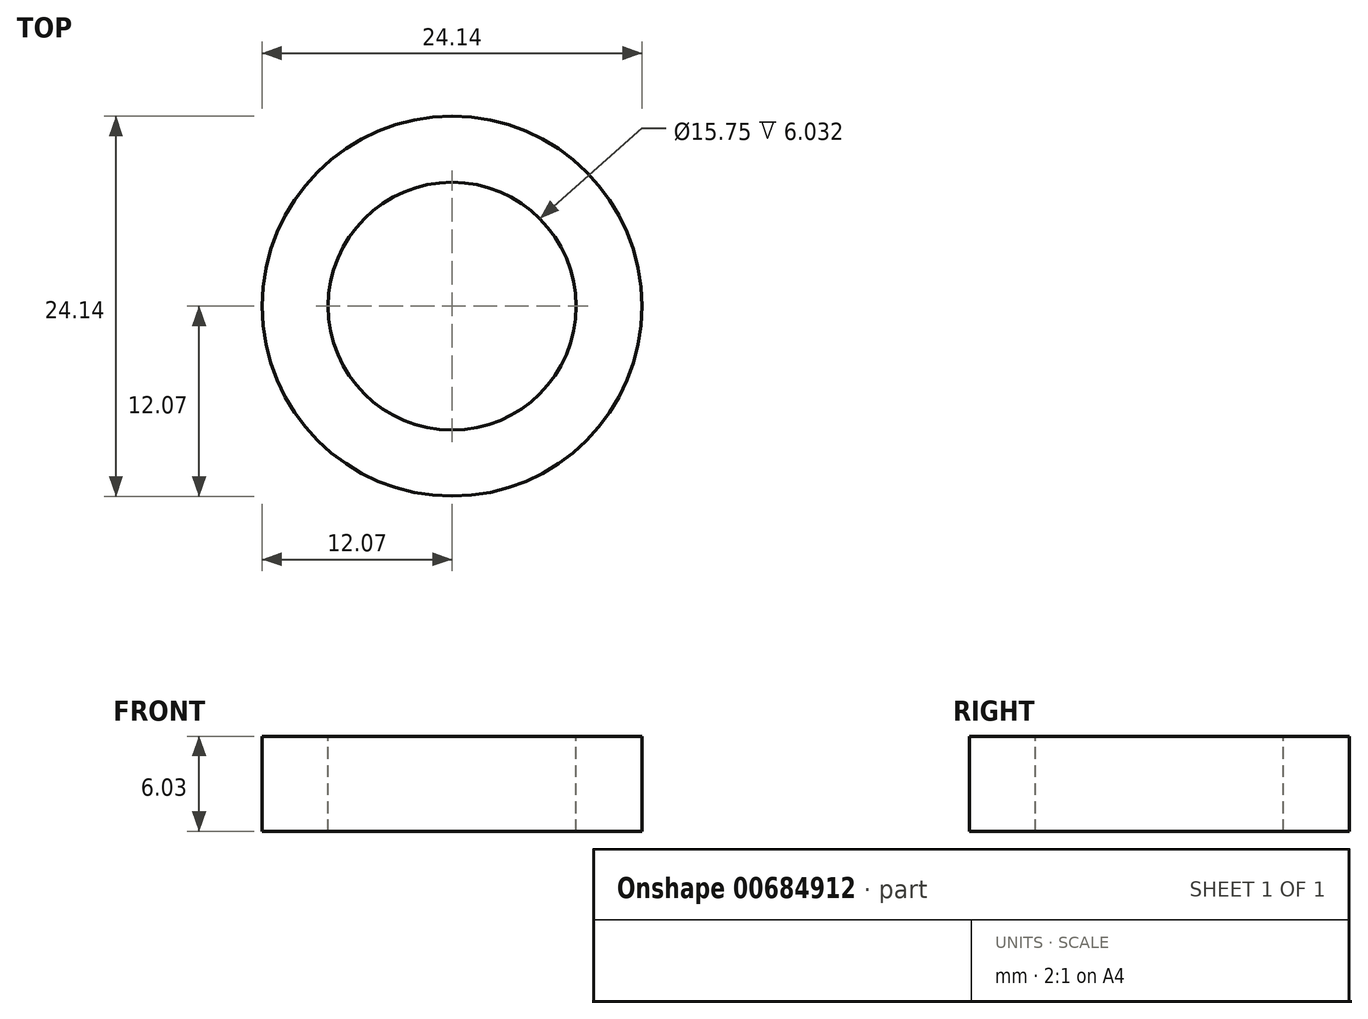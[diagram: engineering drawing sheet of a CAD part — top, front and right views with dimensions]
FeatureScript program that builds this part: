
annotation { "Feature Type Name" : "Feature", "Feature Type Description" : "" }
export const myFeature = defineFeature(function(context is Context, id is Id, definition is map)
    precondition{}
    {
        {
            var Q0;
            Q0=qCreatedBy(makeId("Front.planeOp"),FACE);
            var sketch = newSketch(context, id + "F0", { "sketchPlane" : qUnion([Q0])});
            skLineSegment(sketch, "E0", {"start": v(0, 45.28) * mm, "end": v(0, -44.75) * mm, "construction": true});
            skLineSegment(sketch, "E1", {"start": v(7.87, 0) * mm, "end": v(12.07, 0) * mm});
            skLineSegment(sketch, "E2", {"start": v(12.07, 0) * mm, "end": v(12.07, 6.03) * mm});
            skLineSegment(sketch, "E3", {"start": v(12.07, 6.03) * mm, "end": v(7.87, 6.03) * mm});
            skLineSegment(sketch, "E4", {"start": v(7.87, 6.03) * mm, "end": v(7.87, 0) * mm});
            skSolve(sketch);
        }
        {
            var Q0;
            Q0 = qSketchRegion(id + "F0", true);
            var Q1;
            Q1=sQuery(id+"F0.wireOp",EDGE,"E0");
            revolve(context, id + "F1", {"surfaceOperationType" : NewSurfaceOperationType.NEW, "entities" : qUnion([Q0]), "axis" : qUnion([Q1]), "revolveType" : RevolveType.FULL});
        }
    });
